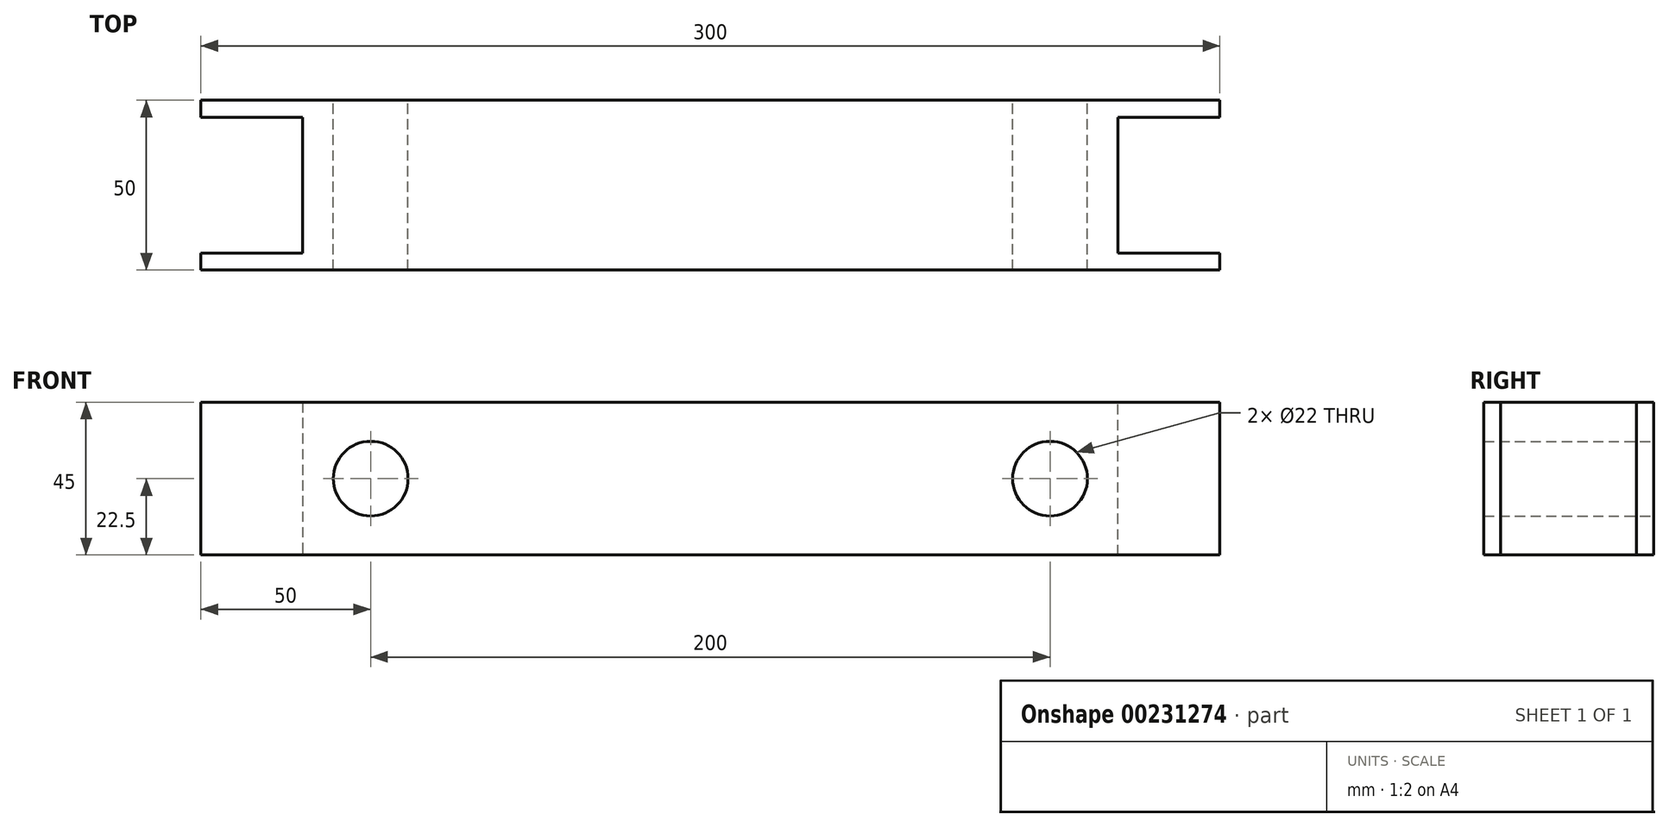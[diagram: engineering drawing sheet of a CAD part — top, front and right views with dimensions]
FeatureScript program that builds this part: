
annotation { "Feature Type Name" : "Feature", "Feature Type Description" : "" }
export const myFeature = defineFeature(function(context is Context, id is Id, definition is map)
    precondition{}
    {
        {
            var Q0;
            Q0=qCreatedBy(makeId("Front.planeOp"),FACE);
            var sketch = newSketch(context, id + "F0", { "sketchPlane" : qUnion([Q0])});
            skLineSegment(sketch, "E0.bottom", {"start": v(150, 22.5) * mm, "end": v(-150, 22.5) * mm});
            skLineSegment(sketch, "E0.top", {"start": v(150, -22.5) * mm, "end": v(-150, -22.5) * mm});
            skLineSegment(sketch, "E0.left", {"start": v(150, 22.5) * mm, "end": v(150, -22.5) * mm});
            skLineSegment(sketch, "E0.right", {"start": v(-150, 22.5) * mm, "end": v(-150, -22.5) * mm});
            skPoint(sketch, "E0.middle", {"position": v(0, 0) * mm});
            skCircle(sketch, "E1", {"center": v(-100, 0) * mm, "radius": 11 * mm});
            skCircle(sketch, "E2.MirrorC", {"center": v(100, 0) * mm, "radius": 11 * mm});
            skSolve(sketch);
        }
        {
            var Q0;
            Q0=makeQuery(id+"F0.imprint","IMPRINT",FACE,{"disambiguationData":[TD([[makeQuery(id+"F0.imprint","IMPRINT",EDGE,{"derivedFrom":sQuery(id+"F0.wireOp",EDGE,"E0.bottom")}),1.0]])]});
            extrude(context, id + "F1", {"entities" : qUnion([Q0]), "depth" : 50 * mm});
        }
        {
            var Q0;
            Q0=makeQuery(id+"F1.opExtrude","SWEPT_FACE",FACE,{"disambiguationData":[OSD([sQuery(id+"F0.wireOp",EDGE,"E0.right")])]});
            var sketch = newSketch(context, id + "F2", { "sketchPlane" : qUnion([Q0])});
            skLineSegment(sketch, "E3.bottom", {"start": v(45, 25) * mm, "end": v(5, 25) * mm});
            skLineSegment(sketch, "E3.top", {"start": v(45, -25) * mm, "end": v(5, -25) * mm});
            skLineSegment(sketch, "E3.left", {"start": v(45, 25) * mm, "end": v(45, -25) * mm});
            skLineSegment(sketch, "E3.right", {"start": v(5, 25) * mm, "end": v(5, -25) * mm});
            skPoint(sketch, "E3.middle", {"position": v(25, 0) * mm});
            skSolve(sketch);
        }
        {
            var Q0;
            {var subQ0=sQuery(id+"F2.wireOp",EDGE,"E3.top");Q0=makeQuery(id+"F2.imprint","IMPRINT",FACE,{"disambiguationData":[TD([[makeQuery(id+"F2.imprint","IMPRINT",EDGE,{"derivedFrom":subQ0}),-1.0]])]});}
            var Q1;
            {var subQ0=sQuery(id+"F2.wireOp",EDGE,"E3.bottom");Q1=makeQuery(id+"F2.imprint","IMPRINT",FACE,{"disambiguationData":[TD([[makeQuery(id+"F2.imprint","IMPRINT",EDGE,{"derivedFrom":subQ0}),1.0]])]});}
            var Q2;
            {var subQ0=sQuery(id+"F2.wireOp",EDGE,"E3.left");var subQ1=sQuery(id+"F0.wireOp",EDGE,"E0.right");var subQ2=makeQuery(id+"F1.opExtrude","SWEPT_EDGE",EDGE,{"disambiguationData":[OSD([sQuery(id+"F0.wireOp",EDGE,"E0.bottom"),subQ1])]});var subQ3=makeQuery(id+"F2.imprint","INTERSECT",VERTEX,{"derivedFrom":[subQ2,subQ0]});Q2=makeQuery(id+"F2.imprint","IMPRINT",FACE,{"disambiguationData":[TD([[makeQuery(id+"F2.imprint","IMPRINT",EDGE,{"disambiguationData":[TD([[subQ3,-1.0]])],"derivedFrom":subQ0}),-1.0]])]});}
            extrude(context, id + "F3", {"entities" : qUnion([Q0, Q1, Q2]), "operationType" : NewBodyOperationType.REMOVE, "oppositeDirection" : true, "depth" : 30 * mm});
        }
        {
            var Q0;
            Q0=makeQuery(id+"F1.opExtrude","SWEPT_FACE",FACE,{"disambiguationData":[OSD([sQuery(id+"F0.wireOp",EDGE,"E0.left")])]});
            var sketch = newSketch(context, id + "F4", { "sketchPlane" : qUnion([Q0])});
            skLineSegment(sketch, "E4.0.0", {"start": v(-45, -22.5) * mm, "end": v(-45, 22.5) * mm});
            skLineSegment(sketch, "E4.0.1", {"start": v(-45, 22.5) * mm, "end": v(-5, 22.5) * mm});
            skLineSegment(sketch, "E4.0.2", {"start": v(-5, 22.5) * mm, "end": v(-5, -22.5) * mm});
            skLineSegment(sketch, "E4.0.3", {"start": v(-5, -22.5) * mm, "end": v(-45, -22.5) * mm});
            skSolve(sketch);
        }
        {
            var Q0;
            Q0=makeQuery(id+"F4.imprint","IMPRINT",FACE,{"disambiguationData":[TD([[makeQuery(id+"F4.imprint","IMPRINT",EDGE,{"derivedFrom":sQuery(id+"F4.wireOp",EDGE,"E4.0.0")}),-1.0]])]});
            extrude(context, id + "F5", {"entities" : qUnion([Q0]), "operationType" : NewBodyOperationType.REMOVE, "oppositeDirection" : true, "depth" : 30 * mm});
        }
    });
